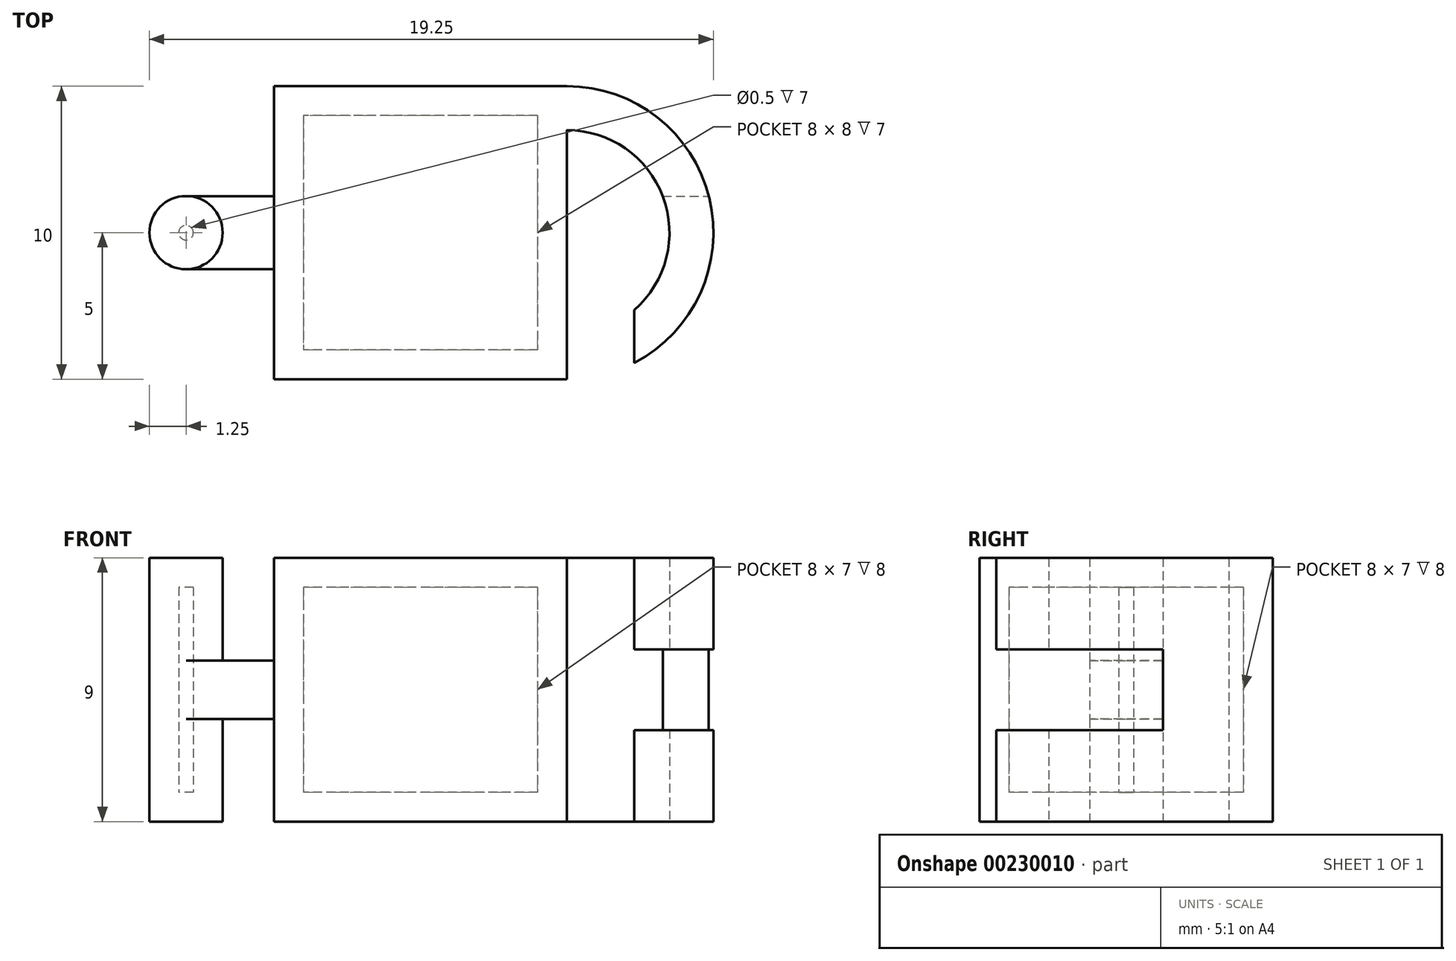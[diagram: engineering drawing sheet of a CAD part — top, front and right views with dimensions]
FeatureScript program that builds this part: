
annotation { "Feature Type Name" : "Feature", "Feature Type Description" : "" }
export const myFeature = defineFeature(function(context is Context, id is Id, definition is map)
    precondition{}
    {
        {
            var Q0;
            Q0=qCreatedBy(makeId("Top.planeOp"),FACE);
            var sketch = newSketch(context, id + "F0", { "sketchPlane" : qUnion([Q0])});
            skLineSegment(sketch, "E0.bottom", {"start": v(10, 10) * mm, "end": v(-10, 10) * mm, "construction": true});
            skLineSegment(sketch, "E0.top", {"start": v(10, -10) * mm, "end": v(-10, -10) * mm, "construction": true});
            skLineSegment(sketch, "E0.left", {"start": v(10, 10) * mm, "end": v(10, -10) * mm, "construction": true});
            skLineSegment(sketch, "E0.right", {"start": v(-10, 10) * mm, "end": v(-10, -10) * mm, "construction": true});
            skPoint(sketch, "E0.middle", {"position": v(0, 0) * mm});
            skLineSegment(sketch, "E1.bottom", {"start": v(-8, 1.25) * mm, "end": v(0, 1.25) * mm});
            skLineSegment(sketch, "E1.top", {"start": v(-8, -1.25) * mm, "end": v(0, -1.25) * mm});
            skLineSegment(sketch, "E1.left", {"start": v(-8, 1.25) * mm, "end": v(-8, -1.25) * mm});
            skCircle(sketch, "E2", {"center": v(-8, 0) * mm, "radius": 1.25 * mm});
            skLineSegment(sketch, "E3.bottom", {"start": v(5, 5) * mm, "end": v(-5, 5) * mm});
            skLineSegment(sketch, "E3.top", {"start": v(5, -5) * mm, "end": v(-5, -5) * mm});
            skLineSegment(sketch, "E3.left", {"start": v(5, 5) * mm, "end": v(5, -5) * mm});
            skLineSegment(sketch, "E3.right", {"start": v(-5, 5) * mm, "end": v(-5, -5) * mm});
            skCircle(sketch, "E4", {"center": v(5, 0) * mm, "radius": 5 * mm});
            skCircle(sketch, "E5.0", {"center": v(5, 0) * mm, "radius": 3.5 * mm});
            skLineSegment(sketch, "E6.bottom", {"start": v(0, 1.25) * mm, "end": v(10, 1.25) * mm});
            skLineSegment(sketch, "E6.top", {"start": v(0, -1.25) * mm, "end": v(10, -1.25) * mm});
            skLineSegment(sketch, "E6.right", {"start": v(10, 1.25) * mm, "end": v(10, -1.25) * mm});
            skLineSegment(sketch, "E7", {"start": v(7.3, -2.64) * mm, "end": v(7.3, -4.44) * mm});
            skSolve(sketch);
        }
        {
            var Q0;
            {var subQ1=sQuery(id+"F0.wireOp",EDGE,"E3.bottom");Q0=makeQuery(id+"F0.imprint","IMPRINT",FACE,{"disambiguationData":[TD([[makeQuery(id+"F0.imprint","IMPRINT",EDGE,{"derivedFrom":subQ1}),1.0]])]});}
            var Q1;
            {var subQ0=sQuery(id+"F0.wireOp",EDGE,"E6.bottom");var subQ6=sQuery(id+"F0.wireOp",EDGE,"E1.bottom");var subQ11=makeQuery(id+"F0.imprint","INTERSECT",VERTEX,{"derivedFrom":[subQ6,subQ0]});Q1=makeQuery(id+"F0.imprint","IMPRINT",FACE,{"disambiguationData":[TD([[makeQuery(id+"F0.imprint","IMPRINT",EDGE,{"disambiguationData":[TD([[subQ11,1.0]])],"derivedFrom":subQ6}),-1.0]])]});}
            var Q2;
            {var subQ1=sQuery(id+"F0.wireOp",EDGE,"E3.top");Q2=makeQuery(id+"F0.imprint","IMPRINT",FACE,{"disambiguationData":[TD([[makeQuery(id+"F0.imprint","IMPRINT",EDGE,{"derivedFrom":subQ1}),-1.0]])]});}
            var Q3;
            {var subQ1=sQuery(id+"F0.wireOp",EDGE,"E3.left");var subQ3=sQuery(id+"F0.wireOp",EDGE,"E5.0");var subQ4=makeQuery(id+"F0.imprint","INTERSECT",VERTEX,{"disambiguationData":[OD(1.0)],"derivedFrom":[subQ1,subQ3]});Q3=makeQuery(id+"F0.imprint","IMPRINT",FACE,{"disambiguationData":[TD([[makeQuery(id+"F0.imprint","IMPRINT",EDGE,{"disambiguationData":[TD([[subQ4,1.0]])],"derivedFrom":subQ3}),-1.0]])]});}
            var Q4;
            {var subQ0=sQuery(id+"F0.wireOp",EDGE,"E6.bottom");var subQ1=sQuery(id+"F0.wireOp",EDGE,"E4");var subQ2=makeQuery(id+"F0.imprint","INTERSECT",VERTEX,{"disambiguationData":[OD(1.0)],"derivedFrom":[subQ1,subQ0]});Q4=makeQuery(id+"F0.imprint","IMPRINT",FACE,{"disambiguationData":[TD([[makeQuery(id+"F0.imprint","IMPRINT",EDGE,{"disambiguationData":[TD([[subQ2,-1.0]])],"derivedFrom":subQ1}),1.0]])]});}
            var Q5;
            {var subQ0=sQuery(id+"F0.wireOp",EDGE,"E5.0");var subQ1=sQuery(id+"F0.wireOp",EDGE,"E3.left");var subQ2=makeQuery(id+"F0.imprint","INTERSECT",VERTEX,{"disambiguationData":[OD(0.0)],"derivedFrom":[subQ1,subQ0]});Q5=makeQuery(id+"F0.imprint","IMPRINT",FACE,{"disambiguationData":[TD([[makeQuery(id+"F0.imprint","IMPRINT",EDGE,{"disambiguationData":[TD([[subQ2,-1.0]])],"derivedFrom":subQ1}),-1.0]])]});}
            var Q6;
            {var subQ0=sQuery(id+"F0.wireOp",EDGE,"E6.bottom");var subQ1=sQuery(id+"F0.wireOp",EDGE,"E3.left");var subQ2=makeQuery(id+"F0.imprint","INTERSECT",VERTEX,{"derivedFrom":[subQ1,subQ0]});Q6=makeQuery(id+"F0.imprint","IMPRINT",FACE,{"disambiguationData":[TD([[makeQuery(id+"F0.imprint","IMPRINT",EDGE,{"disambiguationData":[TD([[subQ2,-1.0]])],"derivedFrom":subQ1}),-1.0]])]});}
            var Q7;
            {var subQ0=sQuery(id+"F0.wireOp",EDGE,"E6.top");var subQ1=sQuery(id+"F0.wireOp",EDGE,"E3.left");var subQ2=makeQuery(id+"F0.imprint","INTERSECT",VERTEX,{"derivedFrom":[subQ1,subQ0]});Q7=makeQuery(id+"F0.imprint","IMPRINT",FACE,{"disambiguationData":[TD([[makeQuery(id+"F0.imprint","IMPRINT",EDGE,{"disambiguationData":[TD([[subQ2,-1.0]])],"derivedFrom":subQ1}),-1.0]])]});}
            var Q8;
            {var subQ1=sQuery(id+"F0.wireOp",EDGE,"E3.left");var subQ3=sQuery(id+"F0.wireOp",EDGE,"E5.0");var subQ4=makeQuery(id+"F0.imprint","INTERSECT",VERTEX,{"disambiguationData":[OD(0.0)],"derivedFrom":[subQ1,subQ3]});Q8=makeQuery(id+"F0.imprint","IMPRINT",FACE,{"disambiguationData":[TD([[makeQuery(id+"F0.imprint","IMPRINT",EDGE,{"disambiguationData":[TD([[subQ4,-1.0]])],"derivedFrom":subQ3}),-1.0]])]});}
            var Q9;
            {var subQ1=sQuery(id+"F0.wireOp",EDGE,"E3.left");var subQ3=sQuery(id+"F0.wireOp",EDGE,"E5.0");var subQ4=makeQuery(id+"F0.imprint","INTERSECT",VERTEX,{"disambiguationData":[OD(0.0)],"derivedFrom":[subQ1,subQ3]});Q9=makeQuery(id+"F0.imprint","IMPRINT",FACE,{"disambiguationData":[TD([[makeQuery(id+"F0.imprint","IMPRINT",EDGE,{"disambiguationData":[TD([[subQ4,1.0]])],"derivedFrom":subQ3}),-1.0]])]});}
            var Q10;
            {var subQ0=sQuery(id+"F0.wireOp",EDGE,"E6.bottom");var subQ1=sQuery(id+"F0.wireOp",EDGE,"E4");var subQ2=makeQuery(id+"F0.imprint","INTERSECT",VERTEX,{"disambiguationData":[OD(0.0)],"derivedFrom":[subQ1,subQ0]});Q10=makeQuery(id+"F0.imprint","IMPRINT",FACE,{"disambiguationData":[TD([[makeQuery(id+"F0.imprint","IMPRINT",EDGE,{"disambiguationData":[TD([[subQ2,1.0]])],"derivedFrom":subQ1}),1.0]])]});}
            var Q11;
            {var subQ0=sQuery(id+"F0.wireOp",EDGE,"E7");Q11=makeQuery(id+"F0.imprint","IMPRINT",FACE,{"disambiguationData":[TD([[makeQuery(id+"F0.imprint","IMPRINT",EDGE,{"derivedFrom":subQ0}),1.0]])]});}
            var Q12;
            {var subQ0=sQuery(id+"F0.wireOp",EDGE,"E1.left");Q12=makeQuery(id+"F0.imprint","IMPRINT",FACE,{"disambiguationData":[TD([[makeQuery(id+"F0.imprint","IMPRINT",EDGE,{"derivedFrom":subQ0}),-1.0]])]});}
            var Q13;
            {var subQ0=sQuery(id+"F0.wireOp",EDGE,"E1.left");Q13=makeQuery(id+"F0.imprint","IMPRINT",FACE,{"disambiguationData":[TD([[makeQuery(id+"F0.imprint","IMPRINT",EDGE,{"derivedFrom":subQ0}),1.0]])]});}
            extrude(context, id + "F1", {"entities" : qUnion([Q0, Q1, Q2, Q3, Q4, Q5, Q6, Q7, Q8, Q9, Q10, Q11, Q12, Q13]), "depth" : 9 * mm, "symmetric" : true});
        }
        {
            var Q0;
            {var subQ2=sQuery(id+"F0.wireOp",EDGE,"E1.bottom");var subQ4=sQuery(id+"F0.wireOp",EDGE,"E3.right");var subQ5=makeQuery(id+"F0.imprint","INTERSECT",VERTEX,{"derivedFrom":[subQ2,subQ4]});Q0=makeQuery(id+"F0.imprint","IMPRINT",FACE,{"disambiguationData":[TD([[makeQuery(id+"F0.imprint","IMPRINT",EDGE,{"disambiguationData":[TD([[subQ5,-1.0]])],"derivedFrom":subQ4}),-1.0]])]});}
            extrude(context, id + "F2", {"entities" : qUnion([Q0]), "operationType" : NewBodyOperationType.ADD, "depth" : 2 * mm, "symmetric" : true});
        }
        {
            var Q0;
            {var subQ0=sQuery(id+"F0.wireOp",EDGE,"E6.bottom");var subQ1=sQuery(id+"F0.wireOp",EDGE,"E4");var subQ2=makeQuery(id+"F0.imprint","INTERSECT",VERTEX,{"disambiguationData":[OD(0.0)],"derivedFrom":[subQ1,subQ0]});Q0=makeQuery(id+"F0.imprint","IMPRINT",FACE,{"disambiguationData":[TD([[makeQuery(id+"F0.imprint","IMPRINT",EDGE,{"disambiguationData":[TD([[subQ2,1.0]])],"derivedFrom":subQ1}),1.0]])]});}
            var Q1;
            {var subQ0=sQuery(id+"F0.wireOp",EDGE,"E7");Q1=makeQuery(id+"F0.imprint","IMPRINT",FACE,{"disambiguationData":[TD([[makeQuery(id+"F0.imprint","IMPRINT",EDGE,{"derivedFrom":subQ0}),1.0]])]});}
            extrude(context, id + "F3", {"entities" : qUnion([Q0, Q1]), "operationType" : NewBodyOperationType.REMOVE, "oppositeDirection" : true, "depth" : 2.75 * mm, "symmetric" : true});
        }
        {
            var Q0;
            Q0=makeQuery(id+"F1.opExtrude","CAP_FACE",FACE,{"disambiguationData":[OSD([sQuery(id+"F0.wireOp",EDGE,"E3.bottom"),sQuery(id+"F0.wireOp",EDGE,"E3.top"),sQuery(id+"F0.wireOp",EDGE,"E3.left"),sQuery(id+"F0.wireOp",EDGE,"E3.right"),sQuery(id+"F0.wireOp",EDGE,"E4"),sQuery(id+"F0.wireOp",EDGE,"E5.0"),sQuery(id+"F0.wireOp",EDGE,"E7")])],"isStart":false});
            var Q1;
            Q1=makeQuery(id+"F1.opExtrude","SWEPT_BODY",BODY,{"disambiguationData":[OSD([sQuery(id+"F0.wireOp",EDGE,"E2")])]});
            shell(context, id + "F4", {"isHollow" : true, "entities" : qUnion([Q0]), "parts" : qUnion([Q1]), "thickness" : 1 * mm});
        }
    });
